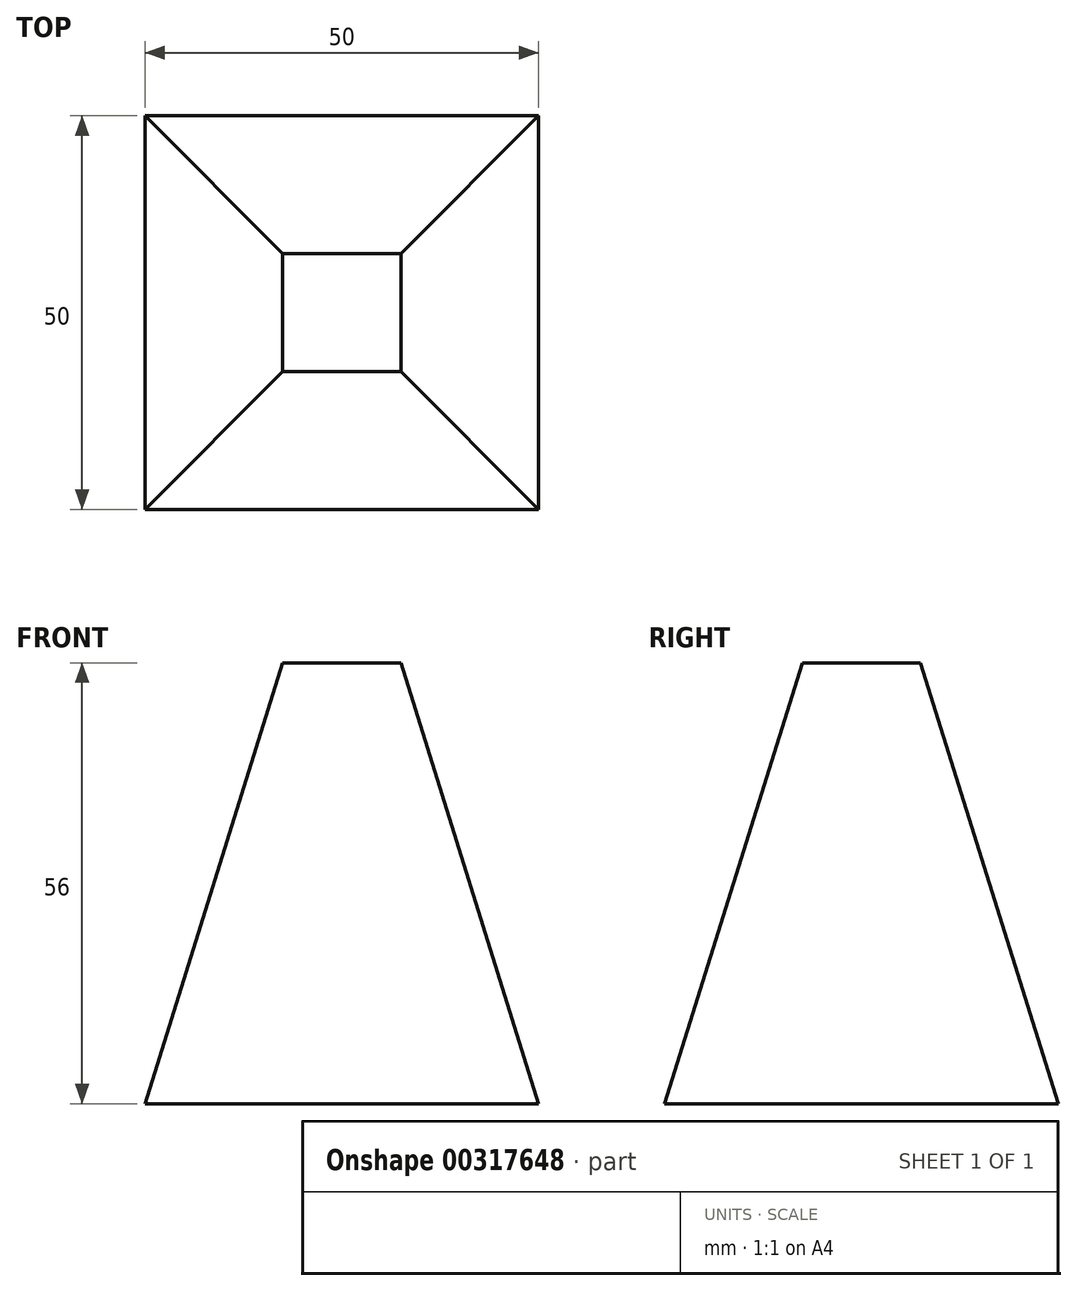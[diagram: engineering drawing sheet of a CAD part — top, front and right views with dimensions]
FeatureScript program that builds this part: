
annotation { "Feature Type Name" : "Feature", "Feature Type Description" : "" }
export const myFeature = defineFeature(function(context is Context, id is Id, definition is map)
    precondition{}
    {
        {
            var Q0;
            Q0=qCreatedBy(makeId("Front.planeOp"),FACE);
            var sketch = newSketch(context, id + "F0", { "sketchPlane" : qUnion([Q0])});
            skLineSegment(sketch, "E0", {"start": v(0, -29.99) * mm, "end": v(0, 26.01) * mm, "construction": true});
            skLineSegment(sketch, "E1", {"start": v(7.5, 26.01) * mm, "end": v(-7.5, 26.01) * mm});
            skLineSegment(sketch, "E2", {"start": v(-25, -29.99) * mm, "end": v(25, -29.99) * mm});
            skLineSegment(sketch, "E3", {"start": v(7.5, 26.01) * mm, "end": v(25, -29.99) * mm});
            skLineSegment(sketch, "E4", {"start": v(-7.5, 26.01) * mm, "end": v(-25, -29.99) * mm});
            skSolve(sketch);
        }
        {
            var Q0;
            Q0 = qSketchRegion(id + "F0", true);
            extrude(context, id + "F1", {"entities" : qUnion([Q0]), "endBound" : BoundingType.SYMMETRIC, "depth" : 50 * mm, "offsetDistance" : 25 * mm});
        }
        {
            var Q0;
            Q0=makeQuery(id+"F1.opExtrude","CAP_EDGE",EDGE,{"disambiguationData":[OSD([sQuery(id+"F0.wireOp",EDGE,"E1")])],"isStart":true});
            var Q1;
            Q1=makeQuery(id+"F1.opExtrude","CAP_EDGE",EDGE,{"disambiguationData":[OSD([sQuery(id+"F0.wireOp",EDGE,"E1")])],"isStart":false});
            chamfer(context, id + "F2", {"entities" : qUnion([Q0, Q1]), "chamferType" : ChamferType.TWO_OFFSETS, "width1" : 17.5 * mm, "oppositeDirection" : false, "width2" : 56 * mm, "tangentPropagation" : true});
        }
    });
